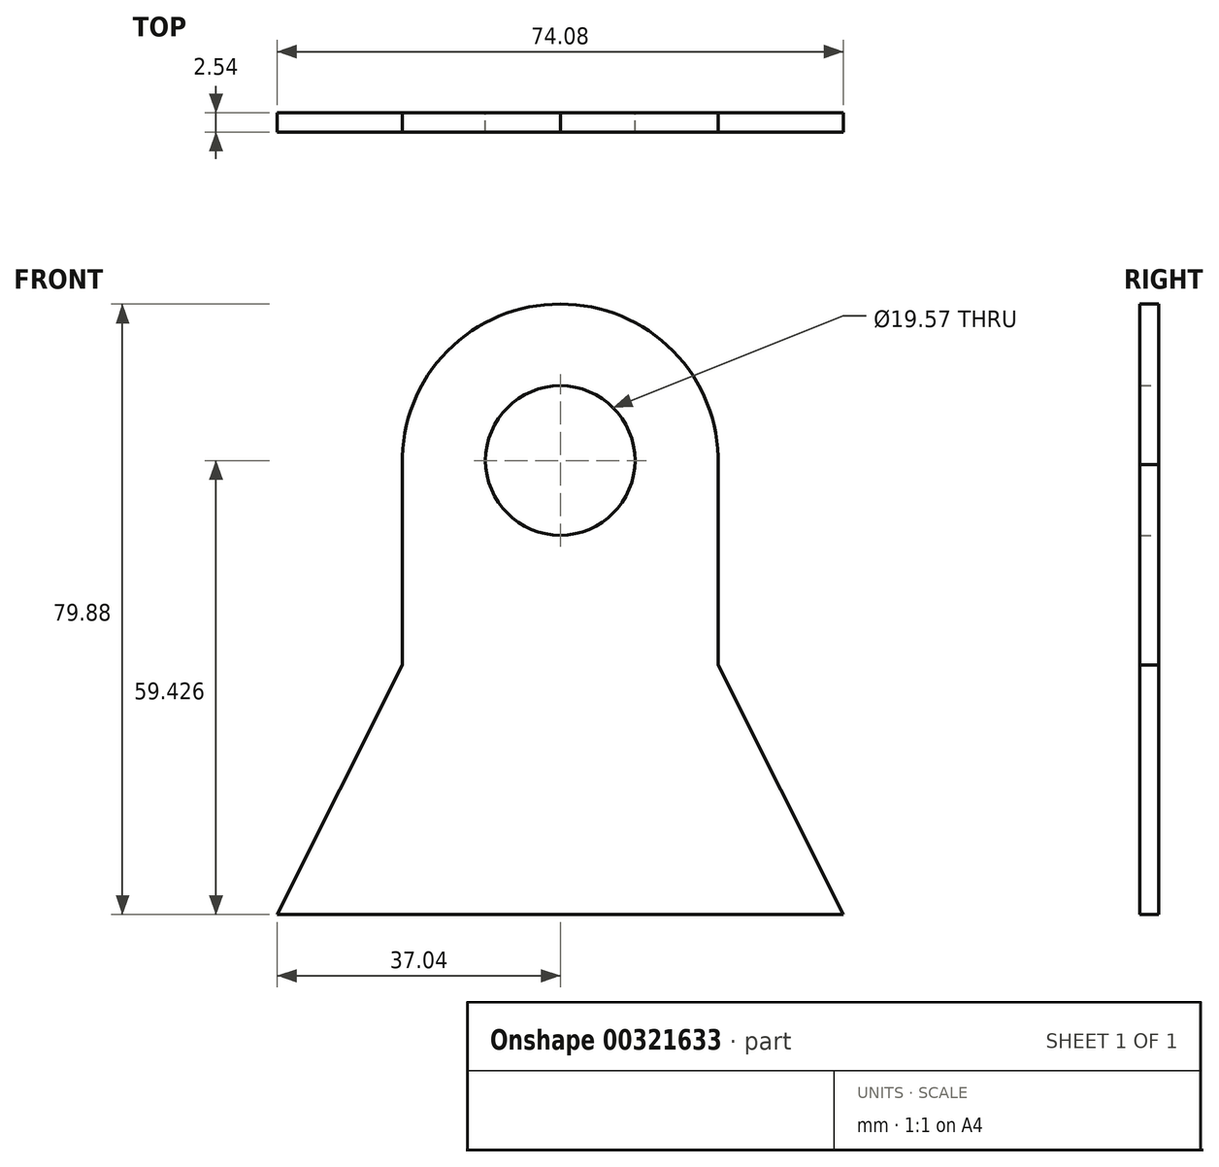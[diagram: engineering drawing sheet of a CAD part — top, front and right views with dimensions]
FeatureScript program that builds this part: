
annotation { "Feature Type Name" : "Feature", "Feature Type Description" : "" }
export const myFeature = defineFeature(function(context is Context, id is Id, definition is map)
    precondition{}
    {
        {
            var Q0;
            Q0=qCreatedBy(makeId("Front.planeOp"),FACE);
            var sketch = newSketch(context, id + "F0", { "sketchPlane" : qUnion([Q0])});
            skCircle(sketch, "E0", {"center": v(0, 26.77) * mm, "radius": 9.79 * mm});
            skArc(sketch, "E1", {"start": v(20.67, 26.23) * mm, "mid": v(0.13, 47.22) * mm, "end": v(-20.4, 26.23) * mm});
            skLineSegment(sketch, "E2", {"start": v(-20.4, 26.23) * mm, "end": v(-19.83, 0) * mm});
            skLineSegment(sketch, "E3", {"start": v(20.67, 26.23) * mm, "end": v(20.67, 0) * mm});
            skLineSegment(sketch, "E4", {"start": v(-36.2, -32.66) * mm, "end": v(37.04, -32.66) * mm});
            skLineSegment(sketch, "E5", {"start": v(37.04, -32.66) * mm, "end": v(20.67, 0) * mm});
            skLineSegment(sketch, "E6", {"start": v(-19.83, 0) * mm, "end": v(-36.2, -32.66) * mm});
            skLineSegment(sketch, "E7", {"start": v(0.13, 26.68) * mm, "end": v(0, -32.66) * mm, "construction": true});
            skCircle(sketch, "E8.MirrorC", {"center": v(0.26, 26.77) * mm, "radius": 9.79 * mm});
            skLineSegment(sketch, "E9.MirrorCS", {"start": v(20.67, 26.14) * mm, "end": v(19.98, -0.09) * mm});
            skArc(sketch, "E10.MirrorCS", {"start": v(-20.41, 26.32) * mm, "mid": v(0.22, 47.22) * mm, "end": v(20.67, 26.14) * mm});
            skSolve(sketch);
        }
        {
            var Q0;
            Q0 = qSketchRegion(id + "F0", true);
            extrude(context, id + "F1", {"entities" : qUnion([Q0]), "depth" : 2.54 * mm});
        }
        {
            var Q0;
            Q0=makeQuery(id+"F1.opExtrude","SWEPT_BODY",BODY,{"disambiguationData":[OSD([sQuery(id+"F0.wireOp",EDGE,"E0"),sQuery(id+"F0.wireOp",EDGE,"E2"),sQuery(id+"F0.wireOp",EDGE,"E3"),sQuery(id+"F0.wireOp",EDGE,"E4"),sQuery(id+"F0.wireOp",EDGE,"E5"),sQuery(id+"F0.wireOp",EDGE,"E6"),sQuery(id+"F0.wireOp",EDGE,"E8.MirrorC"),sQuery(id+"F0.wireOp",EDGE,"E1")])]});
            var Q1;
            Q1=qCreatedBy(makeId("Right.planeOp"),FACE);
            mirror(context, id + "F2", {"operationType" : NewBodyOperationType.ADD, "entities" : qUnion([Q0]), "mirrorPlane" : qUnion([Q1])});
        }
    });
